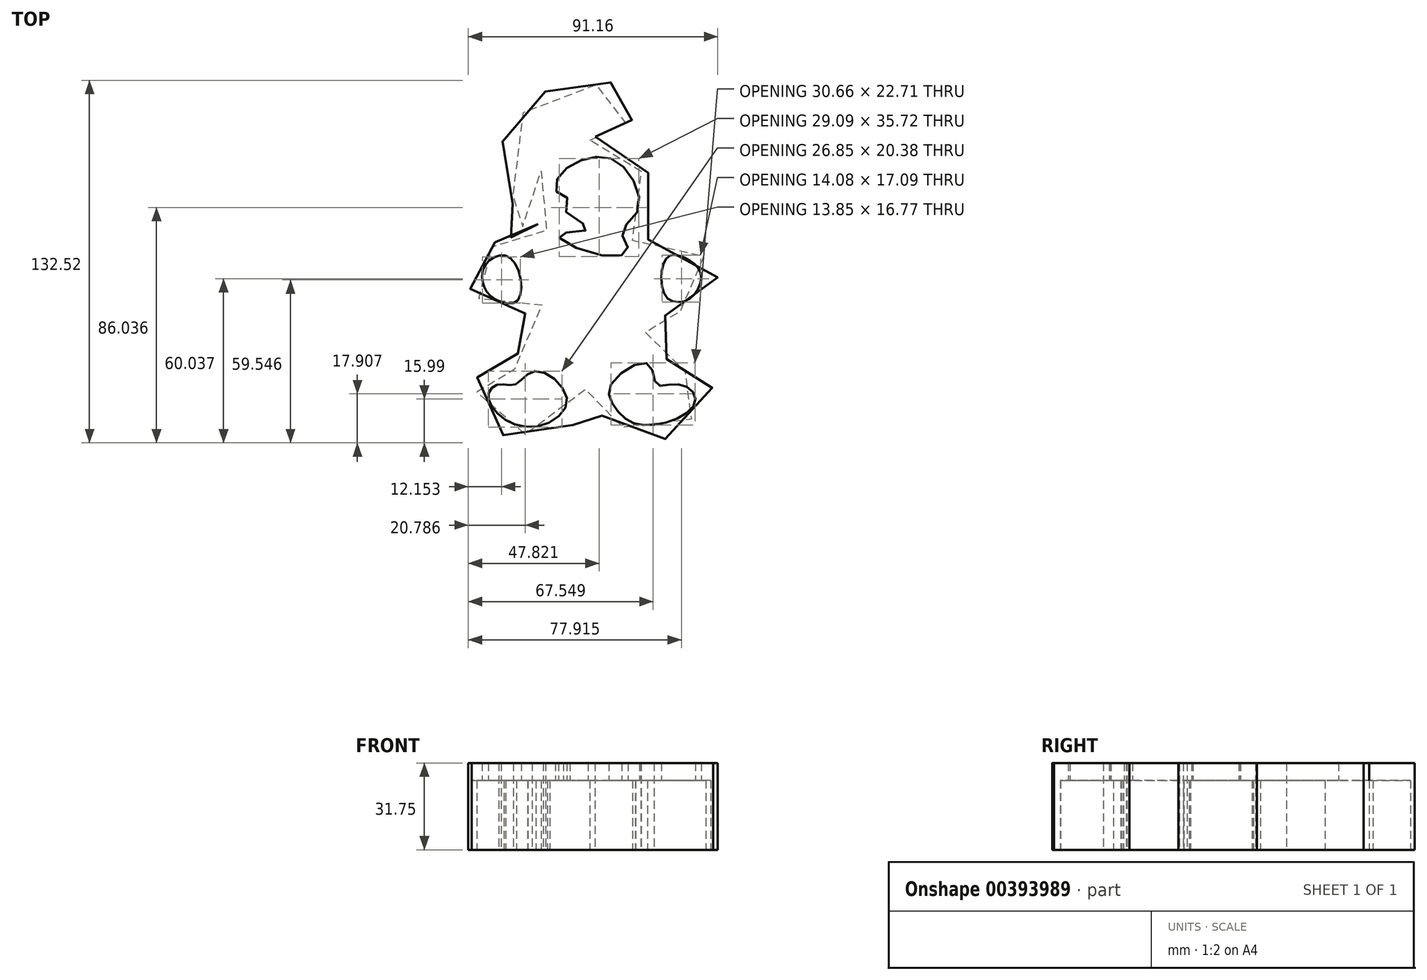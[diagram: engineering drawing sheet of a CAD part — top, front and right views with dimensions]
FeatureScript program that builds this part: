
annotation { "Feature Type Name" : "Feature", "Feature Type Description" : "" }
export const myFeature = defineFeature(function(context is Context, id is Id, definition is map)
    precondition{}
    {
        {
            var Q0;
            Q0=qCreatedBy(makeId("Top.planeOp"),FACE);
            var sketch = newSketch(context, id + "F0", { "sketchPlane" : qUnion([Q0])});
            skFitSpline(sketch, "E0", {"points": [v(3.39, 48.92) * mm, v(4.65, 52.07) * mm, v(7.18, 54.92) * mm, v(13.39, 54.92) * mm, v(14.93, 54.16) * mm, v(19.98, 64.27) * mm, v(16.37, 66.82) * mm, v(8.32, 68.91) * mm, v(-2.11, 68.61) * mm, v(-14.63, 64.14) * mm, v(-23.57, 55.8) * mm, v(-27.44, 43.28) * mm, v(-24.46, 27.78) * mm, v(-24.17, 20.63) * mm, v(-28.04, 14.67) * mm, v(-21.19, 17.35) * mm, v(-19.4, 27.48) * mm, v(-18.2, 34.34) * mm, v(-14.63, 37.91) * mm, v(-15.82, 31.95) * mm, v(-16.12, 24.2) * mm, v(-13.74, 17.65) * mm, v(-11.35, 13.57) * mm, v(-19.05, 11.81) * mm, v(-30.73, 10.38) * mm, v(-35.65, 8.13) * mm, v(-39.63, 1.5) * mm, v(-38.83, -6.34) * mm, v(-35.78, -10.46) * mm, v(-30.34, -13.38) * mm, v(-18.79, -12.45) * mm, v(-12.41, -11.52) * mm, v(-15.6, -19.75) * mm, v(-23.9, -34.25) * mm, v(-25.98, -36.63) * mm, v(-28.96, -35.74) * mm, v(-34.92, -37.23) * mm, v(-37.9, -42.9) * mm, v(-35.81, -49.15) * mm, v(-29.85, -55.1) * mm, v(-19.12, -58.69) * mm, v(-7.2, -56) * mm, v(0.55, -44.98) * mm, v(3.53, -39.31) * mm, v(6.8, -45.27) * mm, v(13.39, -54.51) * mm, v(21.7, -58.39) * mm, v(32.73, -57.5) * mm, v(41.38, -52.13) * mm, v(45.55, -45.87) * mm, v(44.36, -39.31) * mm, v(38.4, -35.74) * mm, v(33.33, -36.33) * mm, v(28.86, -30.07) * mm, v(24.69, -22.92) * mm, v(20.22, -12.5) * mm, v(27.37, -12.5) * mm, v(37.5, -13.38) * mm, v(46.15, -7.72) * mm, v(47.04, 1.81) * mm, v(42.87, 8.67) * mm, v(30.65, 11.81) * mm, v(19.03, 11.81) * mm, v(21.11, 16.12) * mm, v(24.39, 25.66) * mm, v(22, 37.88) * mm, v(16.64, 44.43) * mm, v(10.68, 47.71) * mm, v(3.39, 48.92) * mm]});
            skSolve(sketch);
        }
        {
            var Q0;
            Q0=qCreatedBy(makeId("Top.planeOp"),FACE);
            var sketch = newSketch(context, id + "F1", { "sketchPlane" : qUnion([Q0])});
            skFitSpline(sketch, "E1", {"points": [v(5.31, 50.28) * mm, v(7.67, 53.26) * mm, v(11.78, 53.76) * mm, v(14.52, 52.02) * mm, v(18.87, 56.63) * mm, v(21.85, 63.35) * mm, v(21.23, 66.33) * mm, v(13.27, 69.56) * mm, v(4.3, 70.8) * mm, v(-3.53, 70.05) * mm, v(-13.1, 66.7) * mm, v(-20.44, 61.7) * mm, v(-26.35, 54.45) * mm, v(-29.01, 46.01) * mm, v(-28.57, 38.03) * mm, v(-26.5, 30.04) * mm, v(-24.57, 23.38) * mm, v(-26.78, 18.8) * mm, v(-29.89, 14.35) * mm, v(-28.56, 13.17) * mm, v(-22.05, 14.95) * mm, v(-17.9, 20.57) * mm, v(-17.76, 23.83) * mm, v(-15.84, 18.35) * mm, v(-12.88, 14.36) * mm, v(-20.57, 12.88) * mm, v(-31.52, 11.54) * mm, v(-36.99, 9) * mm, v(-40.77, 2.78) * mm, v(-40.46, -4.94) * mm, v(-37.58, -10.84) * mm, v(-30.82, -14.88) * mm, v(-18.79, -13.92) * mm, v(-13.82, -12.59) * mm, v(-17.64, -20.42) * mm, v(-24.47, -32.02) * mm, v(-26.04, -34.6) * mm, v(-30.46, -33.58) * mm, v(-36.57, -36.3) * mm, v(-39.86, -44.22) * mm, v(-35.55, -52.6) * mm, v(-26.71, -59.74) * mm, v(-14.14, -61.43) * mm, v(-4.63, -57.01) * mm, v(0, -49.88) * mm, v(3.86, -43.08) * mm, v(6.58, -49.53) * mm, v(13.38, -57.34) * mm, v(21.2, -60.74) * mm, v(33.08, -59.71) * mm, v(42.93, -53.6) * mm, v(48.36, -44.08) * mm, v(44.62, -36.27) * mm, v(38.5, -33.55) * mm, v(34.43, -34.23) * mm, v(26.27, -22) * mm, v(22.2, -14.2) * mm, v(31.36, -15.21) * mm, v(42.91, -14.19) * mm, v(49.37, -6.37) * mm, v(48, 5.52) * mm, v(34.39, 13.08) * mm, v(22.18, 12.98) * mm, v(25.23, 19.1) * mm, v(25.23, 35.74) * mm, v(15.71, 47.63) * mm, v(9.6, 49.67) * mm, v(5.31, 50.28) * mm]});
            skSolve(sketch);
        }
        {
            var Q0;
            Q0=makeQuery(id+"F1.imprint","IMPRINT",FACE,{"disambiguationData":[TD([[makeQuery(id+"F1.imprint","IMPRINT",EDGE,{"derivedFrom":sQuery(id+"F1.wireOp",EDGE,"E1")}),1.0]])]});
            var Q1;
            Q1=sQuery(id+"F1.wireOp",EDGE,"E1");
            extrude(context, id + "F2", {"entities" : qUnion([Q0]), "surfaceEntities" : qUnion([Q1]), "depth" : 31.75 * mm});
        }
        {
            var Q0;
            Q0=makeQuery(id+"F0.imprint","IMPRINT",FACE,{"disambiguationData":[TD([[makeQuery(id+"F0.imprint","IMPRINT",EDGE,{"derivedFrom":sQuery(id+"F0.wireOp",EDGE,"E0")}),1.0]])]});
            extrude(context, id + "F3", {"entities" : qUnion([Q0]), "operationType" : NewBodyOperationType.REMOVE, "depth" : 25.4 * mm});
        }
        {
            var Q0;
            Q0=makeQuery(id+"F2.opExtrude","CAP_FACE",FACE,{"disambiguationData":[OSD([sQuery(id+"F1.wireOp",EDGE,"E1")])],"isStart":false});
            var sketch = newSketch(context, id + "F4", { "sketchPlane" : qUnion([Q0])});
            skFitSpline(sketch, "E2", {"points": [v(11.06, 42.2) * mm, v(1.06, 41.86) * mm, v(-7.95, 35.86) * mm, v(-8.28, 29.52) * mm, v(-3.95, 27.18) * mm, v(-6.28, 24.18) * mm, v(2.72, 16.51) * mm, v(-7.95, 14.5) * mm, v(7.4, 6.84) * mm, v(17.26, 9.05) * mm, v(15.07, 15.18) * mm, v(20.74, 22.85) * mm, v(19.07, 34.52) * mm, v(11.06, 42.2) * mm]});
            skSolve(sketch);
        }
        {
            var Q0;
            Q0 = qSketchRegion(id + "F4", true);
            extrude(context, id + "F5", {"entities" : qUnion([Q0]), "operationType" : NewBodyOperationType.REMOVE, "oppositeDirection" : true, "depth" : 25.4 * mm});
        }
        {
            var Q0;
            Q0=makeQuery(id+"F2.opExtrude","CAP_FACE",FACE,{"disambiguationData":[OSD([sQuery(id+"F1.wireOp",EDGE,"E1")])],"isStart":false});
            var sketch = newSketch(context, id + "F6", { "sketchPlane" : qUnion([Q0])});
            skFitSpline(sketch, "E3", {"points": [v(-25.63, 5.84) * mm, v(-22.96, -9.5) * mm, v(-32.3, -8.5) * mm, v(-35.97, -1.5) * mm, v(-33.97, 4.5) * mm, v(-25.63, 5.84) * mm]});
            skSolve(sketch);
        }
        {
            var Q0;
            Q0=makeQuery(id+"F6.imprint","IMPRINT",FACE,{"disambiguationData":[TD([[makeQuery(id+"F6.imprint","IMPRINT",EDGE,{"derivedFrom":sQuery(id+"F6.wireOp",EDGE,"E3")}),1.0]])]});
            var sketch = newSketch(context, id + "F7", { "sketchPlane" : qUnion([Q0])});
            skFitSpline(sketch, "E4", {"points": [v(38, 5.98) * mm, v(31.54, 5.98) * mm, v(31, -8) * mm, v(39.6, -9.08) * mm, v(43.91, 0) * mm, v(38, 5.98) * mm]});
            skFitSpline(sketch, "E5", {"points": [v(-23.84, -40.26) * mm, v(-29.22, -40.26) * mm, v(-33.52, -42.95) * mm, v(-31.37, -49.94) * mm, v(-17.39, -55.86) * mm, v(-5.02, -46.18) * mm, v(-16.31, -35.42) * mm, v(-23.84, -40.26) * mm]});
            skFitSpline(sketch, "E6", {"points": [v(11.1, -40.26) * mm, v(24.55, -32.73) * mm, v(27.78, -40.26) * mm, v(33.7, -40.26) * mm, v(39.92, -42) * mm, v(41.93, -46.21) * mm, v(38, -51.33) * mm, v(26.8, -55.1) * mm, v(18.14, -54) * mm, v(12.14, -48.21) * mm, v(11.1, -40.26) * mm]});
            skSolve(sketch);
        }
        {
            var Q0;
            Q0 = qSketchRegion(id + "F7", true);
            extrude(context, id + "F8", {"entities" : qUnion([Q0]), "operationType" : NewBodyOperationType.REMOVE, "oppositeDirection" : true, "depth" : 25.4 * mm});
        }
        {
            var Q0;
            Q0 = qSketchRegion(id + "F6", true);
            extrude(context, id + "F9", {"entities" : qUnion([Q0]), "operationType" : NewBodyOperationType.REMOVE, "oppositeDirection" : true, "depth" : 25.4 * mm});
        }
    });
